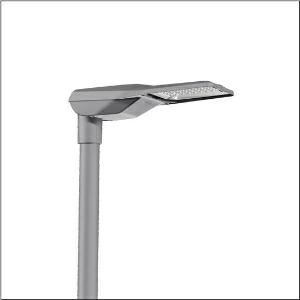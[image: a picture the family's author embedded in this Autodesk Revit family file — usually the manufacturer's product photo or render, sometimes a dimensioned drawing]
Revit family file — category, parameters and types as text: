
# Revit family: streetlight_sl_21_iq_mini___st0_8a_5xe2c41d08jb_a90a
name_source: partatom
category: Lighting Fixtures
units: mm (PartAtom-declared; Revit-internal decimal feet)

## family parameters
Cut with Voids When Loaded = No
Host = Face
Light Source = No
Part Type = Normal
Room Calculation Point = No
Round Connector Dimension = Use Diameter
Shared = No

## types (1)
- --- (1 x LED, 11290 lm, 71.6 W, 4000K)
    Apparent Load = 72 VA
    CIE Flux Codes = 41 75 97 100 100
    Color Rendering = 70
    Color Temperature = 4000K
    Default Elevation = 1800 mm
    Description = Streetlight SL 21 iQ mini, mast luminaire, primary light control with lens, of PMMA, primary optical cover: cover, of toughened safety glass, transparent, light distribution: ST0.8a, light emission: direct distribution, primary light characteristic: asymmetric, installation type: post-top, side-entry, LED, High Power LED, rated luminous flux: 11.290lm, luminous efficacy: 158lm/W, light colour: 740, colour temperature: 4000K, control: Auto-Match, Temp-Guard, Lumen-Switch, Night-Set, Smart-Wire, Light-Fading, Desk-Remote (wireless, voltage-free reading and setting of iQ features in the workshop via application-optimized NFC function/RFID function), optimised constant luminous flux control (CLO 2.0), presetting dimming linear, mains connection: 220..240V, AC, 50/60Hz, start of lifetime: 72W, end of service life: 75W, reduction: 33W, luminaire housing, of diecast aluminium, powder-coated, Siteco® metallic grey (DB 702S), corrosivity category C5 mid according to DIN EN ISO 12944, please order mast flange separately, inclination adjustable: 0°, 5°, 10°, 15°, sealing non-destructively replaceable, multi-level sealing system, length: 628mm, width: 235mm, height: 110mm, mast flange for spigot size: 42mm (side-entry): 5XC10008XM4, 60/48mm (side-entry/post-top): 5XC10108XM2, 76/60mm (side-entry/post-top): 5XC10108XM1, protection rating (complete): IP66, insulation class (complete): insulation class II (safety insulation), certification: CE, ENEC, ENEC+, VDE, impact resistance: IK09, permissible operating ambient temperature for outdoor applications: -40..+50°C, standard-compliant lighting for roads and squares, packaging unit: 1 piece

Light Distribution: ST0.8a
    Height = 110 mm
    Lamp = 1 x LED
    Lamp Light Flux = 11290 lm
    Lamp Power = 71.6 W
    Lamp count = 1
    Length = 625 mm
    Luminous efficacy = 158 lm/W
    Manufacturer = Siteco
    ModVariant = No
    Model = 5XE2C41D08JB
    Number of Poles = 1
    OnlyDefault = Yes
    Power Factor = 1
    Product Name = Streetlight SL 21 iQ mini | ST0.8a
    Product group = mast luminaire | pylon top
    ProductGroupID = 6100
    Protection Class = Protection class II
    Protection Degree = IP 66
    RLX_Detail_Level = 1
    RLX_Emergency_Light_Flux = 0 lm
    RLX_Emergency_Type = 0
    RLX_Emergency_Type_DB = No
    RlxData = <blob elided: 92309 chars, md5=26e3a0fc>
    Socket = socket
    Standby Power = 0 W
    System Light Flux = 11290 lm
    System Power = 72 W
    Type Comments = factory setting: luminous flux: 100 % | dim-lin: 254 | 746 mA
    Type Image = l_1003519.jpg
    URL = http://relux.com
    VarID = @adj_119663
    Voltage = 0 V
    Weight = 0.00 kg
    Width = 234 mm

## geometry (parser evidence)
native form markers: Blend x4, Sweep x10
no freeform markers — native parametric forms only
